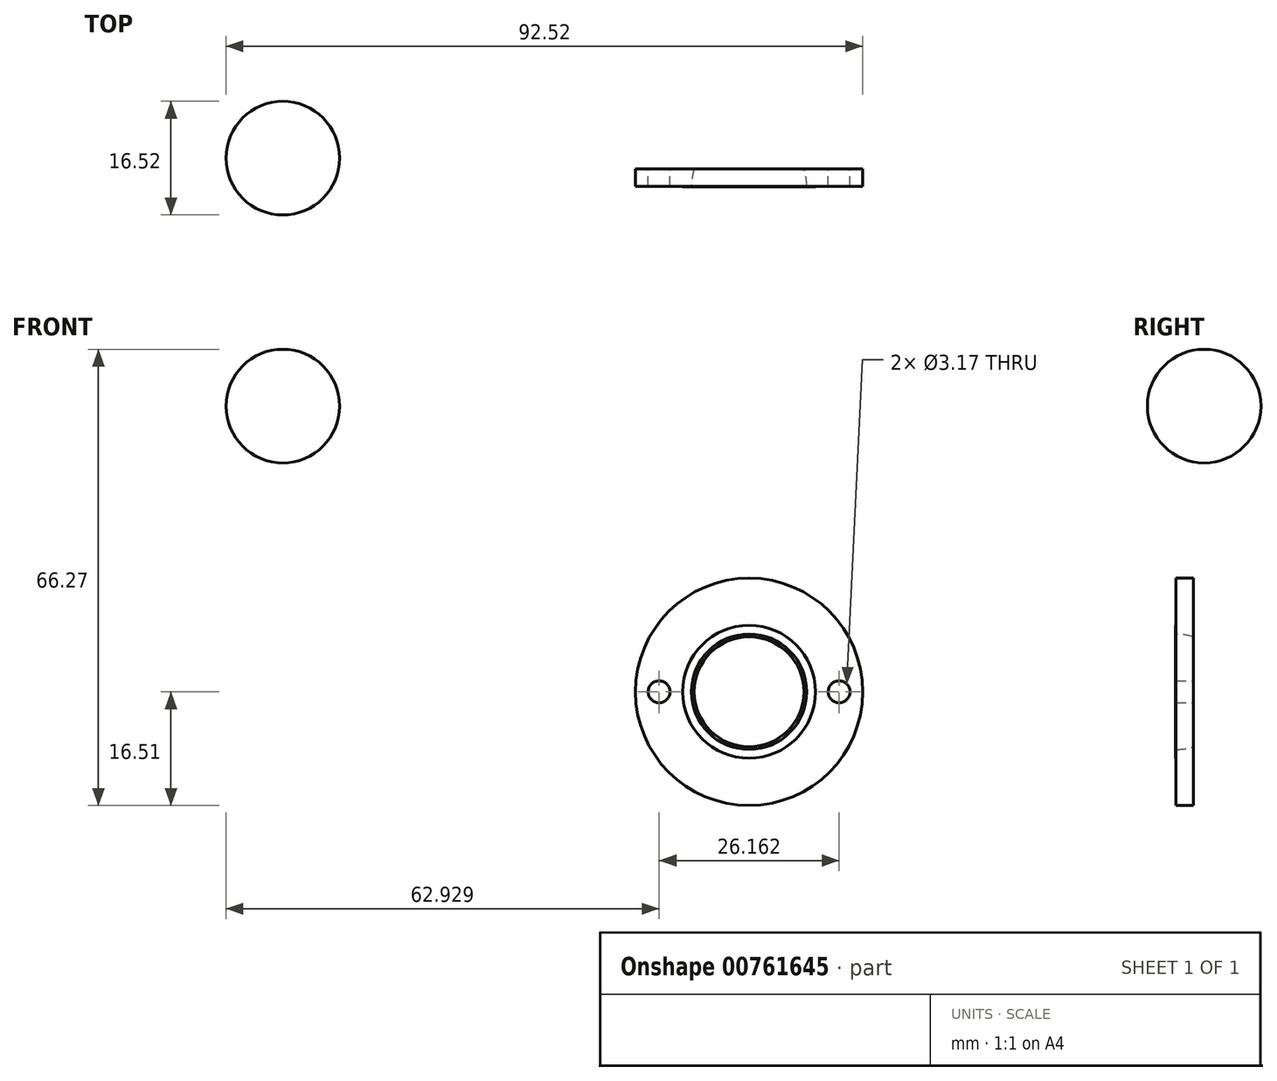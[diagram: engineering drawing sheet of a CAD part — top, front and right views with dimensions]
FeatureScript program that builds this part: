
annotation { "Feature Type Name" : "Feature", "Feature Type Description" : "" }
export const myFeature = defineFeature(function(context is Context, id is Id, definition is map)
    precondition{}
    {
        {
            var Q0;
            Q0=qCreatedBy(makeId("Front.planeOp"),FACE);
            var sketch = newSketch(context, id + "F0", { "sketchPlane" : qUnion([Q0])});
            skCircle(sketch, "E0", {"center": v(0, 0) * mm, "radius": 9.65 * mm});
            skCircle(sketch, "E1", {"center": v(0, 0) * mm, "radius": 16.51 * mm});
            skCircle(sketch, "E2", {"center": v(0, 0) * mm, "radius": 8.38 * mm});
            skLineSegment(sketch, "E3", {"start": v(-16.51, 0) * mm, "end": v(-9.65, 0) * mm});
            skLineSegment(sketch, "E4", {"start": v(9.65, 0) * mm, "end": v(16.51, 0) * mm});
            skCircle(sketch, "E5", {"center": v(-13.08, 0) * mm, "radius": 1.59 * mm});
            skCircle(sketch, "E6", {"center": v(13.08, 0) * mm, "radius": 1.59 * mm});
            skSolve(sketch);
        }
        {
            var Q0;
            Q0=makeQuery(id+"F0.imprint","IMPRINT",FACE,{"disambiguationData":[TD([[makeQuery(id+"F0.imprint","IMPRINT",EDGE,{"derivedFrom":sQuery(id+"F0.wireOp",EDGE,"E0")}),-1.0]])]});
            extrude(context, id + "F1", {"entities" : qUnion([Q0]), "depth" : 4.13 * mm, "offsetDistance" : 25.4 * mm});
        }
        {
            var Q0;
            Q0=makeQuery(id+"F0.imprint","IMPRINT",FACE,{"disambiguationData":[TD([[makeQuery(id+"F0.imprint","IMPRINT",EDGE,{"derivedFrom":sQuery(id+"F0.wireOp",EDGE,"E0")}),1.0]])]});
            var Q1;
            Q1=makeQuery(id+"F0.imprint","IMPRINT",FACE,{"disambiguationData":[TD([[makeQuery(id+"F0.imprint","IMPRINT",EDGE,{"derivedFrom":sQuery(id+"F0.wireOp",EDGE,"E2")}),1.0]])]});
            extrude(context, id + "F2", {"entities" : qUnion([Q0, Q1]), "operationType" : NewBodyOperationType.ADD, "depth" : 4.13 * mm + .65 / 50.8 * mm, "offsetDistance" : 25.4 * mm});
        }
        {
            var Q0;
            Q0=makeQuery(id+"F0.imprint","IMPRINT",FACE,{"disambiguationData":[TD([[makeQuery(id+"F0.imprint","IMPRINT",EDGE,{"derivedFrom":sQuery(id+"F0.wireOp",EDGE,"E0")}),1.0]])]});
            var Q1;
            Q1=makeQuery(id+"F0.imprint","IMPRINT",FACE,{"disambiguationData":[TD([[makeQuery(id+"F0.imprint","IMPRINT",EDGE,{"derivedFrom":sQuery(id+"F0.wireOp",EDGE,"E2")}),1.0]])]});
            var Q2;
            Q2=makeQuery(id+"F0.imprint","IMPRINT",FACE,{"disambiguationData":[TD([[makeQuery(id+"F0.imprint","IMPRINT",EDGE,{"derivedFrom":sQuery(id+"F0.wireOp",EDGE,"E0")}),-1.0]])]});
            extrude(context, id + "F3", {"entities" : qUnion([Q0, Q1, Q2]), "operationType" : NewBodyOperationType.REMOVE, "depth" : 1.59 * mm, "offsetDistance" : 25.4 * mm});
        }
        {
            var Q0;
            Q0=makeQuery(id+"F2.opExtrude","CAP_FACE",FACE,{"disambiguationData":[OSD([sQuery(id+"F0.wireOp",EDGE,"E0"),sQuery(id+"F0.wireOp",EDGE,"E2")])],"isStart":false});
            var sketch = newSketch(context, id + "F4", { "sketchPlane" : qUnion([Q0])});
            skArc(sketch, "E7.0", {"start": v(0, 8.38) * mm, "mid": v(-8.38, 0) * mm, "end": v(0, -8.38) * mm});
            skLineSegment(sketch, "E8", {"start": v(0, 8.38) * mm, "end": v(0, -8.38) * mm});
            skSolve(sketch);
        }
        {
            var Q0;
            Q0=makeQuery(id+"F4.imprint","IMPRINT",FACE,{"disambiguationData":[TD([[makeQuery(id+"F4.imprint","IMPRINT",EDGE,{"derivedFrom":sQuery(id+"F4.wireOp",EDGE,"E7.0")}),1.0]])]});
            var Q1;
            Q1=sQuery(id+"F4.wireOp",EDGE,"E8");
            revolve(context, id + "F5", {"operationType" : NewBodyOperationType.REMOVE, "surfaceOperationType" : NewSurfaceOperationType.NEW, "entities" : qUnion([Q0]), "axis" : qUnion([Q1]), "revolveType" : RevolveType.FULL, "oppositeDirection" : true});
        }
        {
            var Q0;
            Q0=qCreatedBy(makeId("Front.planeOp"),FACE);
            var sketch = newSketch(context, id + "F6", { "sketchPlane" : qUnion([Q0])});
            skArc(sketch, "E9", {"start": v(-67.76, 49.76) * mm, "mid": v(-76.01, 41.5) * mm, "end": v(-67.76, 33.25) * mm});
            skLineSegment(sketch, "E10", {"start": v(-67.76, 49.76) * mm, "end": v(-67.76, 33.25) * mm});
            skSolve(sketch);
        }
        {
            var Q0;
            Q0=makeQuery(id+"F6.imprint","IMPRINT",FACE,{"disambiguationData":[TD([[makeQuery(id+"F6.imprint","IMPRINT",EDGE,{"derivedFrom":sQuery(id+"F6.wireOp",EDGE,"E9")}),1.0]])]});
            var Q1;
            Q1=sQuery(id+"F6.wireOp",EDGE,"E10");
            revolve(context, id + "F7", {"surfaceOperationType" : NewSurfaceOperationType.NEW, "entities" : qUnion([Q0]), "axis" : qUnion([Q1]), "revolveType" : RevolveType.FULL});
        }
    });
